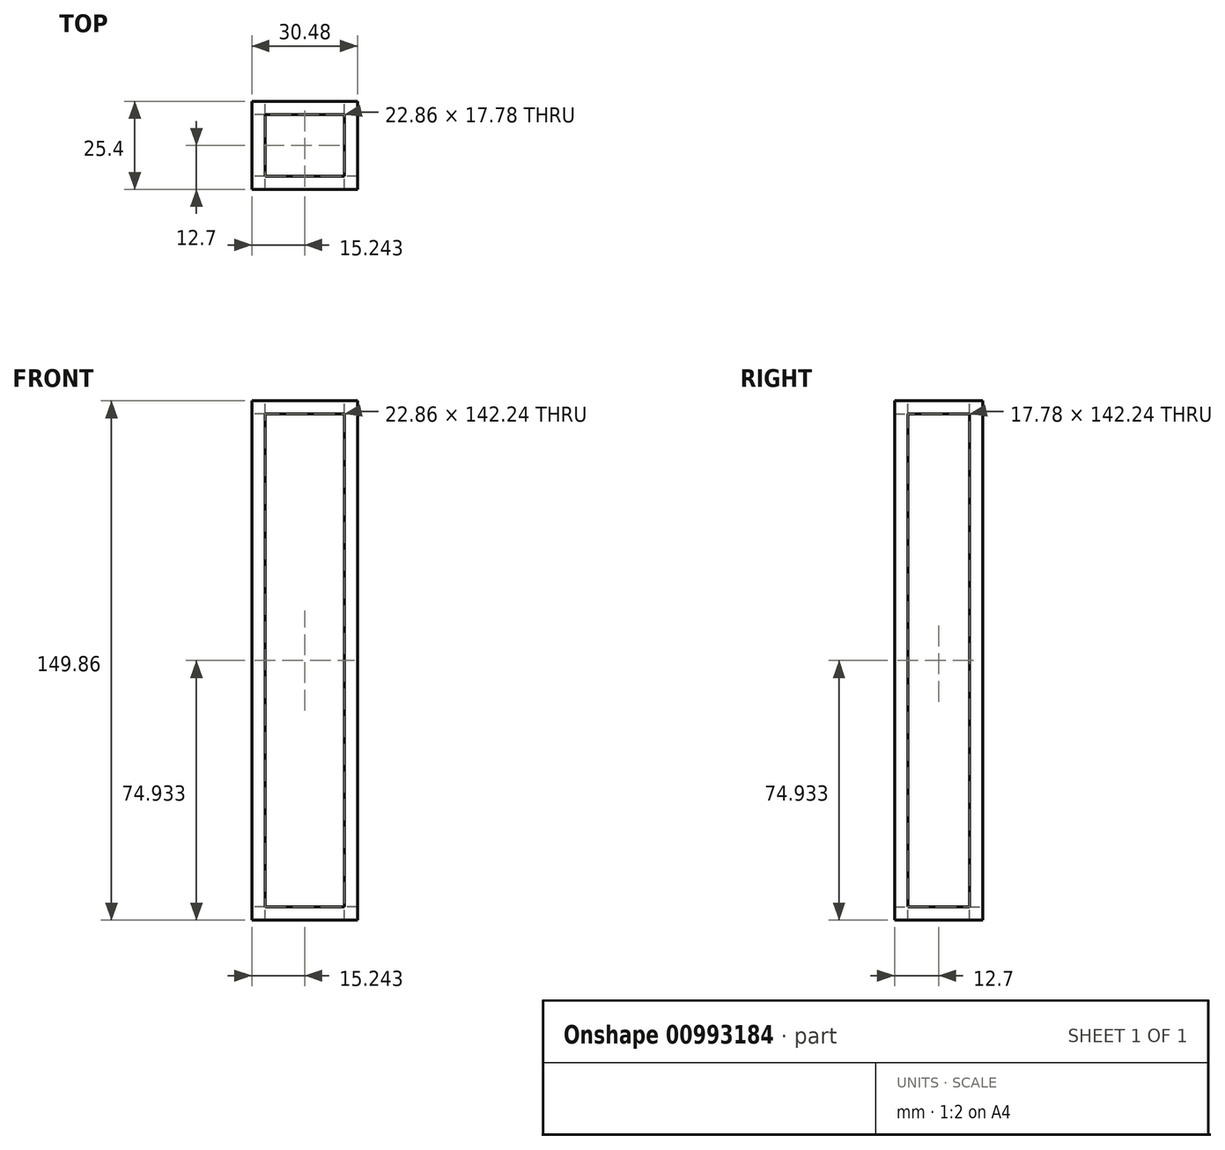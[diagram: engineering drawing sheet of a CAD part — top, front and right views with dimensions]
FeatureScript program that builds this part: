
annotation { "Feature Type Name" : "Feature", "Feature Type Description" : "" }
export const myFeature = defineFeature(function(context is Context, id is Id, definition is map)
    precondition{}
    {
        {
            var Q0;
            Q0=qCreatedBy(makeId("Front.planeOp"),FACE);
            var sketch = newSketch(context, id + "F0", { "sketchPlane" : qUnion([Q0])});
            skLineSegment(sketch, "E0.bottom", {"start": v(-55.94, 87.83) * mm, "end": v(-25.46, 87.83) * mm});
            skLineSegment(sketch, "E0.top", {"start": v(-55.94, -62.03) * mm, "end": v(-25.46, -62.03) * mm});
            skLineSegment(sketch, "E0.left", {"start": v(-55.94, 87.83) * mm, "end": v(-55.94, -62.03) * mm});
            skLineSegment(sketch, "E0.right", {"start": v(-25.46, 87.83) * mm, "end": v(-25.46, -62.03) * mm});
            skLineSegment(sketch, "E1.bottom", {"start": v(-52.13, 84.02) * mm, "end": v(-29.27, 84.02) * mm});
            skLineSegment(sketch, "E1.top", {"start": v(-52.13, -58.22) * mm, "end": v(-29.27, -58.22) * mm});
            skLineSegment(sketch, "E1.left", {"start": v(-52.13, 84.02) * mm, "end": v(-52.13, -58.22) * mm});
            skLineSegment(sketch, "E1.right", {"start": v(-29.27, 84.02) * mm, "end": v(-29.27, -58.22) * mm});
            skSolve(sketch);
        }
        {
            var Q0;
            Q0=makeQuery(id+"F0.imprint","IMPRINT",FACE,{"disambiguationData":[TD([[makeQuery(id+"F0.imprint","IMPRINT",EDGE,{"derivedFrom":sQuery(id+"F0.wireOp",EDGE,"E0.bottom")}),-1.0]])]});
            extrude(context, id + "F1", {"entities" : qUnion([Q0]), "depth" : 25.4 * mm, "offsetDistance" : 25.4 * mm});
        }
        {
            var Q0;
            Q0=makeQuery(id+"F1.opExtrude","SWEPT_FACE",FACE,{"disambiguationData":[OSD([sQuery(id+"F0.wireOp",EDGE,"E0.left")])]});
            var sketch = newSketch(context, id + "F2", { "sketchPlane" : qUnion([Q0])});
            skLineSegment(sketch, "E2.bottom", {"start": v(3.81, 84.02) * mm, "end": v(21.59, 84.02) * mm});
            skLineSegment(sketch, "E2.top", {"start": v(3.81, -58.22) * mm, "end": v(21.6, -58.22) * mm});
            skLineSegment(sketch, "E2.left", {"start": v(3.81, 84.02) * mm, "end": v(3.81, -58.22) * mm});
            skLineSegment(sketch, "E2.right", {"start": v(21.59, 84.02) * mm, "end": v(21.6, -58.22) * mm});
            skSolve(sketch);
        }
        {
            var Q0;
            Q0=makeQuery(id+"F2.imprint","IMPRINT",FACE,{"disambiguationData":[TD([[makeQuery(id+"F2.imprint","IMPRINT",EDGE,{"derivedFrom":sQuery(id+"F2.wireOp",EDGE,"E2.bottom")}),-1.0]])]});
            extrude(context, id + "F3", {"entities" : qUnion([Q0]), "operationType" : NewBodyOperationType.REMOVE, "oppositeDirection" : true, "depth" : 53.34 * mm, "offsetDistance" : 25.4 * mm});
        }
        {
            var Q0;
            Q0=makeQuery(id+"F1.opExtrude","SWEPT_FACE",FACE,{"disambiguationData":[OSD([sQuery(id+"F0.wireOp",EDGE,"E0.bottom")])]});
            var sketch = newSketch(context, id + "F4", { "sketchPlane" : qUnion([Q0])});
            skLineSegment(sketch, "E3.bottom", {"start": v(-52.13, -3.81) * mm, "end": v(-29.27, -3.81) * mm});
            skLineSegment(sketch, "E3.top", {"start": v(-52.13, -21.59) * mm, "end": v(-29.27, -21.59) * mm});
            skLineSegment(sketch, "E3.left", {"start": v(-52.13, -3.81) * mm, "end": v(-52.13, -21.59) * mm});
            skLineSegment(sketch, "E3.right", {"start": v(-29.27, -3.81) * mm, "end": v(-29.27, -21.59) * mm});
            skSolve(sketch);
        }
        {
            var Q0;
            Q0=makeQuery(id+"F4.imprint","IMPRINT",FACE,{"disambiguationData":[TD([[makeQuery(id+"F4.imprint","IMPRINT",EDGE,{"derivedFrom":sQuery(id+"F4.wireOp",EDGE,"E3.bottom")}),-1.0]])]});
            extrude(context, id + "F5", {"entities" : qUnion([Q0]), "operationType" : NewBodyOperationType.REMOVE, "oppositeDirection" : true, "depth" : 152.4 * mm, "offsetDistance" : 25.4 * mm});
        }
    });
